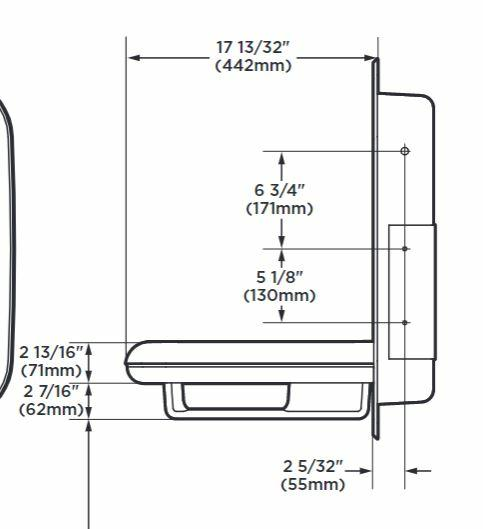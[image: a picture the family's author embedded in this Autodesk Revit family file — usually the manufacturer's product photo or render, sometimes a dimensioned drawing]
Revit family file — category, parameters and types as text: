
# Revit family: KB310-SSWM_Closed
name_source: partatom
category: Specialty Equipment
revit_build: Autodesk Revit 2018 (Build: 20170223_1515(x64)
units: mm (PartAtom-declared; Revit-internal decimal feet)

## family parameters
Cut with Voids When Loaded = No
Host = Face
OmniClass Number = 23.40.20.21
OmniClass Title = Toilet and Bath Specialties
Part Type = Normal
Room Calculation Point = No
Round Connector Dimension = Use Diameter
Shared = Yes

## types (1)
- KB310-SSWM_Closed Position
    ADA Compliant = Yes
    ATS URL = http://www.atsspec.com
    Assembly Code = E2010
    Default Elevation = 23 1/8"
    Description = KB310-SSWM Baby Changing Station Closed Position
    Height = 26 11/32"
    Installation Type = Surface Mounted
    Length = 6 9/16"
    Manufacturer = Koala Kare
    Material = High Density Polyethylene- Koala Kare-Grey
    Model = KB310-SSWM
    Omniclass Table 23 Code = 23.40.20.21
    Omniclass Table 23 Title = Toilet and Bath Specialties
    Price = Prices may vary. Please consult Manufacturer Representative for most up-to-date price list.
    Product Documentation Link = https://f.hubspotusercontent20.net
    Product Page URL = https://info.koalabear.com
    Type Comments = Available Colors: Grey with Stainless Steel
    URL = http://www.koalabear.com
    Warranty Information = 5 Year Limited Warranty
    Width = 41 15/32"

## geometry (parser evidence)
native form markers: Sweep x5
no freeform markers — native parametric forms only
